# Revit family: HVAC_Heat-Pump_Enertech_CTC_CombiAir-6M
name_source: partatom
category: Specialty Equipment
revit_build: Autodesk Revit 2018 (Build: 20170223_1515(x64)
units: mm (PartAtom-declared; Revit-internal decimal feet)

## family parameters
Always vertical = Yes
Cut with Voids When Loaded = No
OmniClass Number = 23.75.00.00
OmniClass Title = Climate Control (HVAC)
Part Type = Normal
Room Calculation Point = No
Round Connector Dimension = Use Diameter
Shared = No
Work Plane-Based = No

## types (1)
- CTC CombiAir 6M
    AirFlow = 2530 m3/h
    AssetType = Fixed
    BIMObjectName = HVAC_Heat-Pump_Enertech_CTC_CombiAir-6M
    Brand = CTC
    CO2Equivalent = 3.130 tonnes
    COP = 5.32
    Capacity = Variable
    Category = Heat Pumps, Air-to-water
    Color = grey
    Cooling capacity A35: W7/W18 = 4.86/7.03
    CoolingCapacity A27: W7/W18 = 5.87/7.98
    Cost = 0 $
    Description = CTC CombiAir 6M, a series of speed-controlled air-to-water heat pumps that adapt to the building’s power demand during the year. For the perfect indoor climate they produce both cooling and heating
    DurationUnit = Year
    EANNumber = 7333077093259
    EER A27: W7/W18 = 3.56/4.52
    EER A35: W7/W18 = 2.61/3.45
    ElectricalDeviceNominalPower = 0 W
    EnergyClassHeatingWithControl = A+++ / A++
    EnergyClassHeatingWithoutControl = A+++ / A++
    EnergyClass_HotWater_TapProfile = A/ L
    GroupFuse = 16 A
    HasProtectiveEarth = Yes
    IP_Code = IP 24
    IfcExportAs = IfcElectricalDeviceCommon
    IfcExportType = HEATER
    InPutPower = 0.50 kW
    Manufacturer = Enertech AB
    ManufacturerCountry = Sweden
    ManufacturerName = Enertech AB
    ManufacturerURL = https://ctc.se
    Material = Steel
    MaxOperatingPressureThermalStore = 4.5 bar
    MaxStartingCurrent = 5 A
    Model = CTC CombiAir 6M
    ModelNumber = 589350001
    NBSDescription = Air to water heat pumps
    NBSReference = 90-40-40/320
    Name = CTC_CombiAir-6M
    NominalCurrent = 0 A
    NominalDepth = 362 mm
    NominalFrequencyRange = 50 Hz
    NominalHeight = 809 mm
    NominalVoltage = 230 V
    NominalWidth = 984 mm  [stored 3.22835 ft]
    NumberOfPoles = 1
    OutputRange = No data
    PhaseAngle = 0.00°
    ProductInformation = CTC CombiAir 6M, a series of speed-controlled air-to-water heat pumps that adapt to the building’s power demand during the year. For the perfect indoor climate they produce both cooling and heating
    PumpMainMaterial = Stainless Steel
    PumpSecondaryMaterial = Brass
    RatedCurrent = 15 A
    RatedHeatOutputModerate = 5 kW
    RatedVoltage = 230 V
    RefrigerantQuantity = 1.50 kg
    RefrigerantType = R410A
    SCOPCold = 3.68
    SCOPModerate = 4.79
    SCOPWarm = 6.39
    Shape = Rectangular
    Size = 364x993x791 mm
    Sound pressureLPA 10m = 25 dB
    Sound pressureLPA 5m = 31 dB
    SoundPowerLWA = 50 dB
    SpecifiedOutput = 5 kW
    Touchscreen = no
    UNSPSCCode = 40101806
    URL = https://ctc-heating.com
    Uniclass2 = Pr_40_70_65
    Uniclass2015Description = Preparation catering equipment
    Uniclass2015Reference = Pr_40_70_65
    UsageCurrent = 0 A
    Version = 1
    VersionDate = 24/05/2022
    WarrantyDurationUnit = Year
    WaterVolumeHeathingSystem = No data
    Weight = 67 kg

note: [stored X ft] marks values corroborated as IEEE doubles in the binary element streams (Revit-internal decimal feet)

## geometry (parser evidence)
native form markers: Sweep x4
no freeform markers — native parametric forms only
